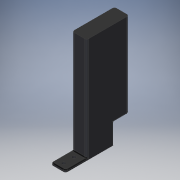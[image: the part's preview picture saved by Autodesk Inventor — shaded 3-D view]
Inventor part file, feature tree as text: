
AUTODESK INVENTOR PART (.ipt)
format: ipt  version: 2018 (Build 220112000, 112)  size: 428,544 bytes
history: native  units: mm
features: reference x7, sketch x5, extrude x5, fillet x5, other x4, projected_geometry x3, plane x2
ambient origin geometry x8: Origin, YZ Plane, XZ Plane, XY Plane, X Axis, Y Axis, Z Axis, Center Point
bodies: Solid1 (feature_tree)
feature tree (31):
  sketch  "Sketch1"  dims[d0=40.0mm d1=10.0mm d2=0.0mm]
  plane  "Work Plane1"
  extrude  "Extrusion1"  Depth=10.0mm TaperAngle=0.0deg
  sketch  "Sketch2"  dims[d3=80.0mm d4=40.0mm]
  plane  "Work Plane2"
  extrude  "Extrusion2"  Depth=40.0mm
  extrude  "Extrusion3"  Depth=10.0mm TaperAngle=0.0deg
  extrude  "Extrusion4"  Depth=80.0mm
  fillet  "Fillet1"  Radius=40.0mm
  fillet  "Fillet2"  Radius=20.0mm
  fillet  "Fillet3"  Radius=80.0mm
  fillet  "Fillet4"  Radius=5.0mm
  fillet  "Fillet5"  Radius=3.0mm
  extrude  "Extrusion5"  Depth=10.0mm
  reference  "Reference1"
  reference  "Reference2"
  reference  "Reference3"
  reference  "Reference4"
  sketch  "Sketch3"  dims[d5=20.0mm d6=10.0mm d7=0.0mm]
  projected_geometry  "Projected Loop1"
  projected_geometry  "Projected Loop2"
  reference  "Reference5"
  sketch  "Sketch5"  dims[d8=80.0mm d9=80.0mm d10=40.0mm d11=20.0mm d12=80.0mm d13=0.0mm d15=5.0mm d16=3.0mm]
  projected_geometry  "Projected Loop3"
  reference  "Reference6"
  sketch  "Sketch6"  dims[d17=5.0mm d18=3.0mm d19=50.0mm d20=0.0mm d21=2.0mm d22=1.0mm d23=1.0mm d24=1.0mm d25=1.0mm d26=21.79mm d27=10.0mm d28=0.0mm d29=3.0mm d30=3.0mm]
  reference  "Reference7"
  other  "<userpath>\OneDrive\Documents\Inventor\TSA\2018\Animatronics\Tortoise\TurtleAssembly2.iam"
  other  "TurtleAssembly2.iam"
  other  "Frame - Copy:1"
  other  "holder_gear_mount:1"
